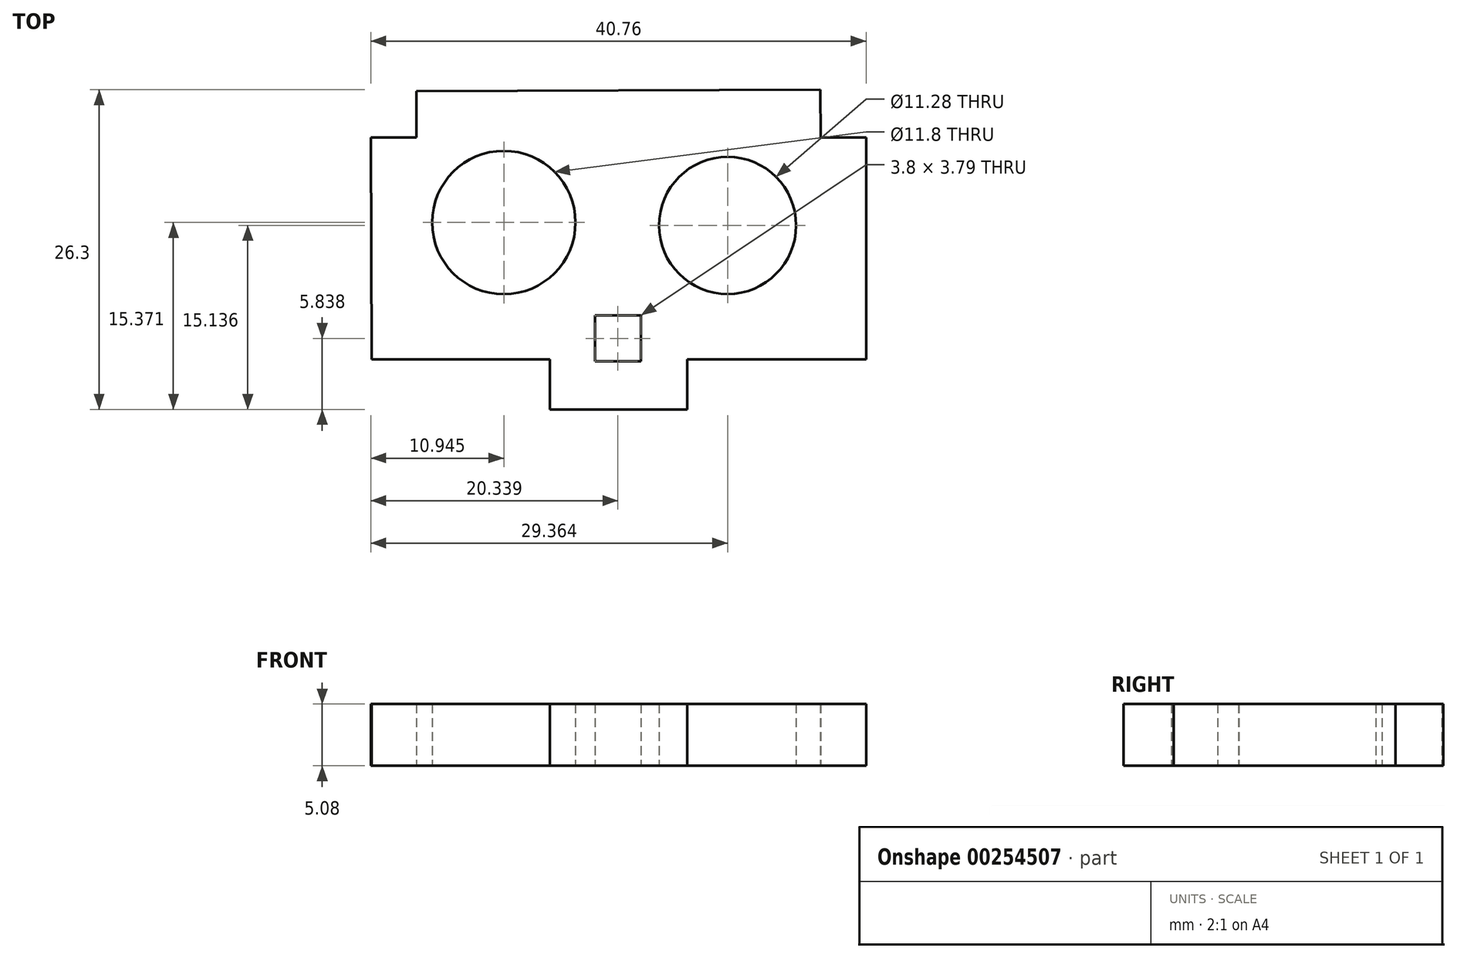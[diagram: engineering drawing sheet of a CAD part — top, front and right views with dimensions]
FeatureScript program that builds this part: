
annotation { "Feature Type Name" : "Feature", "Feature Type Description" : "" }
export const myFeature = defineFeature(function(context is Context, id is Id, definition is map)
    precondition{}
    {
        {
            var Q0;
            Q0=qCreatedBy(makeId("Top.planeOp"),FACE);
            var sketch = newSketch(context, id + "F0", { "sketchPlane" : qUnion([Q0])});
            skLineSegment(sketch, "E0", {"start": v(-33.45, 9.2) * mm, "end": v(-26.8, 16.12) * mm});
            skLineSegment(sketch, "E1", {"start": v(-26.8, 16.12) * mm, "end": v(-22.17, 16.12) * mm});
            skLineSegment(sketch, "E2", {"start": v(-22.17, 16.12) * mm, "end": v(-22.17, 19.99) * mm});
            skLineSegment(sketch, "E3", {"start": v(-22.17, 19.99) * mm, "end": v(-25.8, 19.97) * mm});
            skLineSegment(sketch, "E4", {"start": v(-25.8, 19.97) * mm, "end": v(-25.8, 38.73) * mm});
            skLineSegment(sketch, "E5", {"start": v(-25.8, 38.73) * mm, "end": v(-18.88, 45.9) * mm});
            skLineSegment(sketch, "E6", {"start": v(-18.88, 45.9) * mm, "end": v(14.3, 45.9) * mm});
            skLineSegment(sketch, "E7", {"start": v(14.3, 45.9) * mm, "end": v(22.2, 38.73) * mm});
            skLineSegment(sketch, "E8", {"start": v(22.2, 38.73) * mm, "end": v(22.2, 19.97) * mm});
            skLineSegment(sketch, "E9", {"start": v(22.2, 19.97) * mm, "end": v(18.52, 19.97) * mm});
            skLineSegment(sketch, "E10", {"start": v(18.52, 19.97) * mm, "end": v(18.52, 16.12) * mm});
            skLineSegment(sketch, "E11", {"start": v(18.52, 16.12) * mm, "end": v(22.2, 16.12) * mm});
            skLineSegment(sketch, "E12", {"start": v(22.2, 16.12) * mm, "end": v(29.83, 9.43) * mm});
            skLineSegment(sketch, "E13", {"start": v(29.83, 9.43) * mm, "end": v(29.83, -20.85) * mm});
            skLineSegment(sketch, "E14", {"start": v(29.83, -20.85) * mm, "end": v(22.14, -20.85) * mm});
            skLineSegment(sketch, "E15", {"start": v(22.14, -20.85) * mm, "end": v(22.14, -32.04) * mm});
            skLineSegment(sketch, "E16", {"start": v(22.14, -32.04) * mm, "end": v(19.03, -35.7) * mm});
            skLineSegment(sketch, "E17", {"start": v(19.03, -35.7) * mm, "end": v(3.87, -35.7) * mm});
            skLineSegment(sketch, "E18", {"start": v(3.87, -35.7) * mm, "end": v(3.87, -28.47) * mm});
            skLineSegment(sketch, "E19", {"start": v(3.87, -28.47) * mm, "end": v(-7.29, -28.47) * mm});
            skLineSegment(sketch, "E20", {"start": v(-7.29, -28.47) * mm, "end": v(-7.29, -35.7) * mm});
            skLineSegment(sketch, "E21", {"start": v(-7.29, -35.7) * mm, "end": v(-23.05, -35.7) * mm});
            skLineSegment(sketch, "E22", {"start": v(-23.05, -35.7) * mm, "end": v(-25.8, -32.44) * mm});
            skLineSegment(sketch, "E23", {"start": v(-25.8, -32.44) * mm, "end": v(-25.8, -20.85) * mm});
            skLineSegment(sketch, "E24", {"start": v(-25.8, -20.85) * mm, "end": v(-33.32, -20.85) * mm});
            skLineSegment(sketch, "E25", {"start": v(-33.32, -20.85) * mm, "end": v(-33.45, 9.2) * mm});
            skCircle(sketch, "E26", {"center": v(-11.3, 31.23) * mm, "radius": 5.9 * mm});
            skPoint(sketch, "E26.first.point", {"position": v(-17.19, 30.94) * mm});
            skPoint(sketch, "E26.second.point", {"position": v(-5.4, 31.07) * mm});
            skPoint(sketch, "E26.third.point", {"position": v(-11.26, 25.33) * mm});
            skCircle(sketch, "E27", {"center": v(7.12, 31) * mm, "radius": 5.64 * mm});
            skPoint(sketch, "E27.first.point", {"position": v(1.48, 30.84) * mm});
            skPoint(sketch, "E27.second.point", {"position": v(12.76, 30.78) * mm});
            skPoint(sketch, "E27.third.point", {"position": v(7.1, 36.64) * mm});
            skLineSegment(sketch, "E28.bottom", {"start": v(-14.96, 34.57) * mm, "end": v(-7.5, 34.57) * mm});
            skLineSegment(sketch, "E28.top", {"start": v(-14.96, 27.44) * mm, "end": v(-7.5, 27.44) * mm});
            skLineSegment(sketch, "E28.left", {"start": v(-14.96, 34.57) * mm, "end": v(-14.96, 27.44) * mm});
            skLineSegment(sketch, "E28.right", {"start": v(-7.5, 34.57) * mm, "end": v(-7.5, 27.44) * mm});
            skLineSegment(sketch, "E29.bottom", {"start": v(3.8, 34.28) * mm, "end": v(10.72, 34.28) * mm});
            skLineSegment(sketch, "E29.top", {"start": v(3.8, 27.44) * mm, "end": v(10.72, 27.44) * mm});
            skLineSegment(sketch, "E29.left", {"start": v(3.8, 34.28) * mm, "end": v(3.8, 27.44) * mm});
            skLineSegment(sketch, "E29.right", {"start": v(10.72, 34.28) * mm, "end": v(10.72, 27.44) * mm});
            skLineSegment(sketch, "E30.bottom", {"start": v(7.12, 31) * mm, "end": v(3.8, 31) * mm});
            skLineSegment(sketch, "E30.top", {"start": v(7.12, 34.28) * mm, "end": v(3.8, 34.28) * mm});
            skLineSegment(sketch, "E30.left", {"start": v(7.12, 31) * mm, "end": v(7.12, 34.28) * mm});
            skLineSegment(sketch, "E30.right", {"start": v(3.8, 31) * mm, "end": v(3.8, 34.28) * mm});
            skLineSegment(sketch, "E31.bottom", {"start": v(-11.3, 31.23) * mm, "end": v(-14.96, 31.23) * mm});
            skLineSegment(sketch, "E31.top", {"start": v(-11.3, 34.57) * mm, "end": v(-14.96, 34.57) * mm});
            skLineSegment(sketch, "E31.left", {"start": v(-11.3, 31.23) * mm, "end": v(-11.3, 34.57) * mm});
            skLineSegment(sketch, "E31.right", {"start": v(-14.96, 31.23) * mm, "end": v(-14.96, 34.57) * mm});
            skLineSegment(sketch, "E32.bottom", {"start": v(-3.8, 23.6) * mm, "end": v(0, 23.6) * mm});
            skLineSegment(sketch, "E32.top", {"start": v(-3.8, 19.8) * mm, "end": v(0, 19.8) * mm});
            skLineSegment(sketch, "E32.left", {"start": v(-3.8, 23.6) * mm, "end": v(-3.8, 19.8) * mm});
            skLineSegment(sketch, "E32.right", {"start": v(0, 23.6) * mm, "end": v(0, 19.8) * mm});
            skLineSegment(sketch, "E33.bottom", {"start": v(-7.5, 15.86) * mm, "end": v(3.8, 15.86) * mm});
            skLineSegment(sketch, "E33.top", {"start": v(-7.5, 12.27) * mm, "end": v(3.8, 12.27) * mm});
            skLineSegment(sketch, "E33.left", {"start": v(-7.5, 15.86) * mm, "end": v(-7.5, 12.27) * mm});
            skLineSegment(sketch, "E33.right", {"start": v(3.8, 15.86) * mm, "end": v(3.8, 12.27) * mm});
            skPoint(sketch, "E34.oppositeSnap0", {"position": v(-25.8, -26.64) * mm});
            skLineSegment(sketch, "E34.bottom", {"start": v(-29.45, -9.9) * mm, "end": v(-25.8, -9.9) * mm});
            skLineSegment(sketch, "E34.top", {"start": v(-29.45, -17.27) * mm, "end": v(-25.8, -17.27) * mm});
            skLineSegment(sketch, "E34.left", {"start": v(-29.45, -9.9) * mm, "end": v(-29.45, -17.27) * mm});
            skLineSegment(sketch, "E34.right", {"start": v(-25.8, -9.9) * mm, "end": v(-25.8, -17.27) * mm});
            skLineSegment(sketch, "E35.top", {"start": v(-29.45, 8.74) * mm, "end": v(-25.8, 8.74) * mm});
            skLineSegment(sketch, "E35.left", {"start": v(-29.45, -9.9) * mm, "end": v(-29.45, 8.74) * mm});
            skLineSegment(sketch, "E35.right", {"start": v(-25.8, -9.9) * mm, "end": v(-25.8, 8.74) * mm});
            skLineSegment(sketch, "E36.bottom", {"start": v(22.2, -9.9) * mm, "end": v(25.76, -9.9) * mm});
            skLineSegment(sketch, "E36.top", {"start": v(22.2, -17.27) * mm, "end": v(25.76, -17.27) * mm});
            skLineSegment(sketch, "E36.left", {"start": v(22.2, -9.9) * mm, "end": v(22.2, -17.27) * mm});
            skLineSegment(sketch, "E36.right", {"start": v(25.76, -9.9) * mm, "end": v(25.76, -17.27) * mm});
            skLineSegment(sketch, "E37.top", {"start": v(22.2, 8.7) * mm, "end": v(25.76, 8.7) * mm});
            skLineSegment(sketch, "E37.left", {"start": v(22.2, -9.9) * mm, "end": v(22.2, 8.7) * mm});
            skLineSegment(sketch, "E37.right", {"start": v(25.76, -9.9) * mm, "end": v(25.76, 8.7) * mm});
            skLineSegment(sketch, "E38.bottom", {"start": v(-3.6, -28.47) * mm, "end": v(0, -28.47) * mm});
            skLineSegment(sketch, "E38.top", {"start": v(-3.6, -24.74) * mm, "end": v(0, -24.74) * mm});
            skLineSegment(sketch, "E38.left", {"start": v(-3.6, -28.47) * mm, "end": v(-3.6, -24.74) * mm});
            skLineSegment(sketch, "E38.right", {"start": v(0, -28.47) * mm, "end": v(0, -24.74) * mm});
            skLineSegment(sketch, "E39", {"start": v(-22.24, -24.61) * mm, "end": v(-22.24, -31.85) * mm});
            skLineSegment(sketch, "E40", {"start": v(-22.24, -31.85) * mm, "end": v(-11.06, -31.85) * mm});
            skLineSegment(sketch, "E41", {"start": v(-11.06, -31.85) * mm, "end": v(-11.06, -28.48) * mm});
            skLineSegment(sketch, "E42", {"start": v(-11.06, -28.48) * mm, "end": v(-7.29, -28.47) * mm});
            skLineSegment(sketch, "E43", {"start": v(-7.29, -24.61) * mm, "end": v(-22.24, -24.61) * mm});
            skLineSegment(sketch, "E44", {"start": v(-7.29, -24.61) * mm, "end": v(-7.29, -28.47) * mm});
            skLineSegment(sketch, "E45", {"start": v(3.87, -28.47) * mm, "end": v(3.87, -24.61) * mm});
            skLineSegment(sketch, "E46", {"start": v(3.87, -24.61) * mm, "end": v(18.56, -24.61) * mm});
            skLineSegment(sketch, "E47", {"start": v(18.56, -24.61) * mm, "end": v(18.56, -31.97) * mm});
            skLineSegment(sketch, "E48", {"start": v(18.56, -31.97) * mm, "end": v(7.4, -31.97) * mm});
            skLineSegment(sketch, "E49", {"start": v(7.4, -31.97) * mm, "end": v(7.4, -28.47) * mm});
            skLineSegment(sketch, "E50", {"start": v(7.4, -28.47) * mm, "end": v(3.87, -28.47) * mm});
            skLineSegment(sketch, "E51", {"start": v(-22.17, 19.99) * mm, "end": v(-22.24, 38.23) * mm});
            skLineSegment(sketch, "E52", {"start": v(-22.24, 38.23) * mm, "end": v(-18.48, 38.25) * mm});
            skLineSegment(sketch, "E53", {"start": v(-18.48, 38.25) * mm, "end": v(-18.5, 42.04) * mm});
            skLineSegment(sketch, "E54", {"start": v(-18.5, 42.04) * mm, "end": v(14.76, 42.16) * mm});
            skLineSegment(sketch, "E55", {"start": v(14.76, 42.16) * mm, "end": v(14.78, 38.23) * mm});
            skLineSegment(sketch, "E56", {"start": v(14.78, 38.23) * mm, "end": v(18.52, 38.24) * mm});
            skLineSegment(sketch, "E57", {"start": v(18.52, 38.24) * mm, "end": v(18.52, 19.97) * mm});
            skLineSegment(sketch, "E58", {"start": v(3.8, 15.86) * mm, "end": v(3.8, 19.97) * mm});
            skLineSegment(sketch, "E59", {"start": v(3.8, 19.97) * mm, "end": v(18.52, 19.97) * mm});
            skLineSegment(sketch, "E60", {"start": v(-7.5, 15.86) * mm, "end": v(-7.5, 19.99) * mm});
            skLineSegment(sketch, "E61", {"start": v(-7.5, 19.99) * mm, "end": v(-22.17, 19.99) * mm});
            skLineSegment(sketch, "E62", {"start": v(-22.23, 12.38) * mm, "end": v(-22.23, -21.38) * mm});
            skLineSegment(sketch, "E63", {"start": v(-22.23, -21.38) * mm, "end": v(18.48, -21.38) * mm});
            skLineSegment(sketch, "E64", {"start": v(18.48, -21.38) * mm, "end": v(18.48, 12.34) * mm});
            skLineSegment(sketch, "E65", {"start": v(18.48, 12.34) * mm, "end": v(14.65, 12.34) * mm});
            skLineSegment(sketch, "E66", {"start": v(14.65, 12.34) * mm, "end": v(14.65, 15.86) * mm});
            skLineSegment(sketch, "E67", {"start": v(14.65, 15.86) * mm, "end": v(3.8, 15.86) * mm});
            skLineSegment(sketch, "E68", {"start": v(-22.23, 12.38) * mm, "end": v(-18.53, 12.38) * mm});
            skLineSegment(sketch, "E69", {"start": v(-18.53, 12.38) * mm, "end": v(-18.53, 15.86) * mm});
            skLineSegment(sketch, "E70", {"start": v(-18.53, 15.86) * mm, "end": v(-7.5, 15.86) * mm});
            skLineSegment(sketch, "E71.bottom", {"start": v(-7.42, -28.31) * mm, "end": v(-7.13, -28.31) * mm});
            skLineSegment(sketch, "E71.top", {"start": v(-7.42, -28.63) * mm, "end": v(-7.13, -28.63) * mm});
            skLineSegment(sketch, "E71.left", {"start": v(-7.42, -28.31) * mm, "end": v(-7.42, -28.63) * mm});
            skLineSegment(sketch, "E71.right", {"start": v(-7.13, -28.31) * mm, "end": v(-7.13, -28.63) * mm});
            skLineSegment(sketch, "E72.bottom", {"start": v(3.95, -28.38) * mm, "end": v(3.78, -28.38) * mm});
            skLineSegment(sketch, "E72.top", {"start": v(3.95, -28.56) * mm, "end": v(3.78, -28.56) * mm});
            skLineSegment(sketch, "E72.left", {"start": v(3.95, -28.38) * mm, "end": v(3.95, -28.56) * mm});
            skLineSegment(sketch, "E72.right", {"start": v(3.78, -28.38) * mm, "end": v(3.78, -28.56) * mm});
            skSolve(sketch);
        }
        {
            var Q0;
            Q0=makeQuery(id+"F0.imprint","IMPRINT",FACE,{"disambiguationData":[TD([[makeQuery(id+"F0.imprint","IMPRINT",EDGE,{"derivedFrom":sQuery(id+"F0.wireOp",EDGE,"E26")}),-1.0]])]});
            extrude(context, id + "F1", {"entities" : qUnion([Q0]), "depth" : 5.08 * mm});
        }
    });
